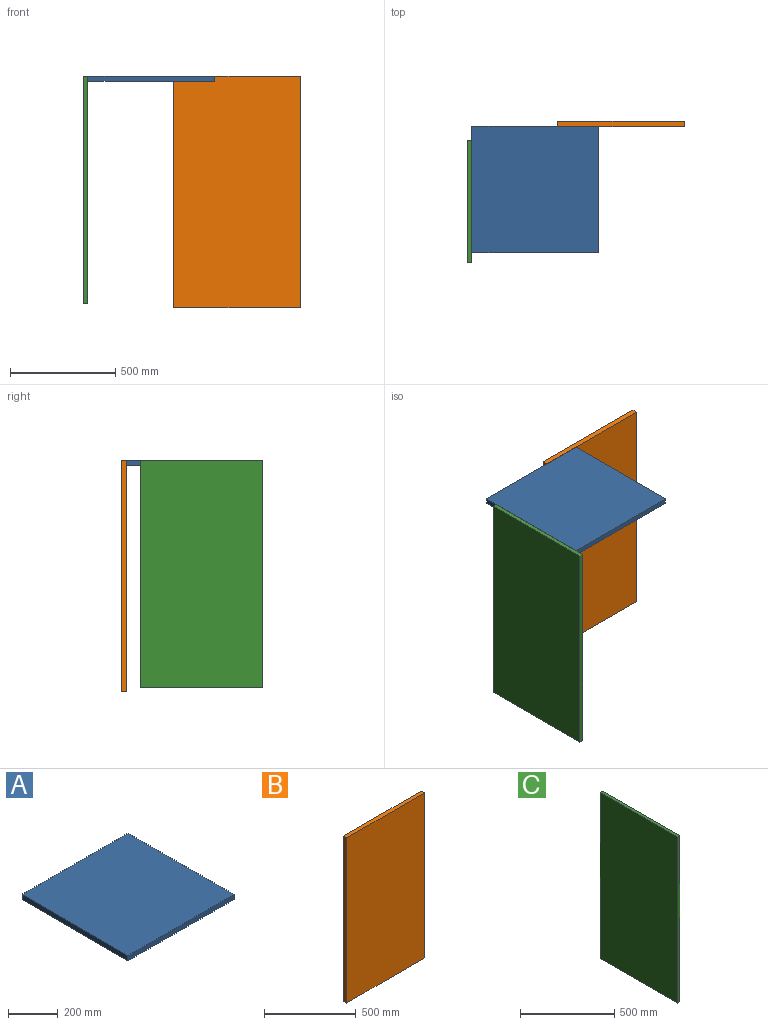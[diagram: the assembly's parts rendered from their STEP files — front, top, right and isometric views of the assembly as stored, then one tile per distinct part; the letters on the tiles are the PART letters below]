
ASSEMBLY  parts=3 mates=4
PART A: 6 faces, bbox 600x600x25 mm
  f0: plane 600x25mm, normal (1,0,0), area 15000mm2, adj f1,f3,f4,f5
  f1: plane 600x25mm, normal (0,1,0), area 15000mm2, adj f0,f2,f4,f5
  f2: plane 600x25mm, normal (-1,0,0), area 15000mm2, adj f1,f3,f4,f5
  f3: plane 600x25mm, normal (0,-1,0), area 15000mm2, adj f0,f2,f4,f5
  f4: plane 600x600mm, normal (0,0,-1), area 360000mm2, adj f0,f1,f2,f3
  f5: plane 600x600mm, normal (0,0,1), area 360000mm2, adj f0,f1,f2,f3
PART B: 6 faces, bbox 600x25x1100 mm
  f0: plane 1100x25mm, normal (1,0,0), area 27500mm2, adj f1,f3,f4,f5
  f1: plane 600x25mm, normal (0,0,1), area 15000mm2, adj f0,f2,f4,f5
  f2: plane 1100x25mm, normal (-1,0,0), area 27500mm2, adj f1,f3,f4,f5
  f3: plane 600x25mm, normal (0,0,-1), area 15000mm2, adj f0,f2,f4,f5
  f4: plane 1100x600mm, normal (0,-1,0), area 660000mm2, adj f0,f1,f2,f3
  f5: plane 1100x600mm, normal (0,1,0), area 660000mm2, adj f0,f1,f2,f3
PART C: 6 faces, bbox 20x580x1080 mm
  f0: plane 1080x20mm, normal (0,1,0), area 21600mm2, adj f1,f3,f4,f5
  f1: plane 580x20mm, normal (0,0,1), area 11600mm2, adj f0,f2,f4,f5
  f2: plane 1080x20mm, normal (0,-1,0), area 21600mm2, adj f1,f3,f4,f5
  f3: plane 580x20mm, normal (0,0,-1), area 11600mm2, adj f0,f2,f4,f5
  f4: plane 1080x580mm, normal (1,0,0), area 626400mm2, adj f0,f1,f2,f3
  f5: plane 1080x580mm, normal (-1,0,0), area 626400mm2, adj f0,f1,f2,f3
PLACE A rot(axis=(0,1,0),180deg) t=(355.24,19.66,864.41)mm
PLACE B t=(762.46,344.66,314.41)mm
PLACE C t=(35.24,-35.48,324.41)mm
MATE planar A.f4 <-> B.f1  axis (0,0,1) through (355.24,19.66,864.41)mm
MATE planar A.f1 <-> B.f4  axis (0,1,0) through (355.24,319.66,851.91)mm
MATE planar C.f1 <-> A.f4  axis (0,0,1) through (45.24,-35.48,864.41)mm
MATE planar C.f4 <-> A.f0  axis (1,0,0) through (55.24,-35.48,324.41)mm
